# Revit family: result
name_source: partatom
category: Mechanical Equipment
units: mm (PartAtom-declared; Revit-internal decimal feet)

## family parameters
Always vertical = Yes
Cut with Voids When Loaded = No
Maintain Annotation Orientation = No
OmniClass Number = 23.75.00.00
OmniClass Title = Climate Control (HVAC)
Part Type = Normal
Room Calculation Point = No
Round Connector Dimension = Use Radius
Shared = No
Work Plane-Based = No

## types (1)
- -1-ALTAIR 120 V RE  - Heat Recovery Units
    AcquisitionDate = 0
    Arrangement = 0
    ArticleNumber = 0
    AssemblyPlace = 0
    AssessmentCondition = 0
    AssessmentDate = 0
    AssessmentDescription = 0
    AtmosphericAcidification = 0
    AtmosphericAcidificationPerUnit = 0
    Autor = Bimetica Parametric Design Services, S.L.
    BIMElementExpiryDate = 0
    BIMElementIssueDate = 2025-07-10
    BIMElementVersion = 1.0
    COBieCategory = 0
    ClimateChange = 0
    ClimateChangePerUnit = 0
    ConductorFunction = 0
    Connector Radius 1 = 47 mm  [stored 0.154199 ft]
    Connector Radius 2 = 47 mm  [stored 0.154199 ft]
    ContainerMaterial = 0
    CorrienteNominal = 0 A
    Default Elevation = 0 mm  [stored 0 ft]
    Description = Mechanical Ventilation Heat Recovery Unit with a high-efficiency heat exchanger to provide a constant supply of fresh tempered air into the living spaces.The incorporated intelligent humidity tracking control as standard, constantly monitor the humidity level, meaning no user intervention required.As humidity rises and falls, the motor speed adjusts in direct correlation.This controls IAQ quietly and efficiently, reducing the periods of time when the system operates on maximum speed, saving energy.Our constant flow technology delivers the required airflow at all times. The ultra compact design allows installation of the unit vertically on the wall.ALTAIR is equipped with high efficieny G4 filters for supply and extract.The included remote controller, allows the user to select the working mode of the unit (manual or automatic) and indicates when the filter needs replacing.It is advisable to use LAF silencers (accessory not included):&nbsp;LAF 95 for the ALTAIR-120 model.The ALTAIR unit can communicate with the home automation system via Modbus or other gateway protocols.By means of the SPCM Lite M communications board, the ALTAIR unit communicates with the CONNECTAIR platform, which allows it to be remotely controlled.Features- Counterflow heat exchanger with efficiency up to 88%.- Low consumption EC motor.- Centrifugal fans with forward bladed impeller.- Modbus connection.- EPP body.- 4 inlets Ø100 mm (ALTAIR 120).- Delivery filter:&nbsp;G4 (ISO coarse 65%).&nbsp;Optional M5 (ISO ePM10 50%).&nbsp;Extraction filter G4 (ISO coarse 65%).
    DiametroImpulsor = 0 mm  [stored 0 ft]
    Dimension 1 = Yes
    Dimension 2 = No
    DirectionOfRotation = 0
    DischargePosition = 0
    DischargePressureLoss = 0.0 Pa
    DischargeVelocity = 0.0 m/s
    DrivePowerLoss = 0 W
    EfficiencyCurve = 0
    Eutrophication = 0
    EutrophicationPerUnit = 0
    Exclusions = 0
    ExpectedServiceLife = 0
    FanEfficiency = 0
    FanPowerRate = 0 W
    HasProtectiveEarth = Yes
    HazardousWaste = 0
    HazardousWastePerUnit = 0
    IFCClassification = Fans
    IndiceFlujoNominal = 0.0 L/s
    IndicePotenciaNominal = 0 W
    InertWaste = 0
    InertWastePerUnit = 0
    InstallationDate = 0
    InsulationStandardClass = 0
    IsExtendedWarranty = No
    LifeCyclePhase = 0
    MaintenanceCertificate = 0
    MaintenanceCost = 0
    MaintenanceFrequency = 0
    MaintenanceRegulation = 0
    MaintenanceSpecifications = 0
    MaintenanceTask = 0
    MaintenanceUnit = 0
    Manufacturer = ELEKTRODESIGN VENTILATORY, SPOL.S.R.O.
    MasterformatCodigo = 23 00 00
    MasterformatTitulo = Heating, Ventilating, and Air Conditioning (HVAC)
    Material Carcasa = Steel, Galvanized painted white
    Material Conector Bornes = Plastic, Formed white
    MaterialHousing B = Steel, Galvanized painted black
    MaterialHousing C = Plastic, Formed Black
    MeanTimeBetweenFailure = 0
    Model = 0
    ModelLabel = 0
    NominalFrequencyRange = 0 Hz
    NonHazardousWaste = 0
    NonHazardousWastePerUnit = 0
    NonRenewableEnergyConsumption = 0
    NonRenewableEnergyConsumptionPerUnit = 0
    NumeroPolos = 1
    OmniclassCodigo = 23-33 31 19
    OmniclassTitulo = Fans
    OperationTemperatureRange = 0
    OperationalCriteria = 0
    OverallEfficiency = 0
    PA = 77 mm  [stored 0.252625 ft]
    PB = 360 mm  [stored 1.1811 ft]
    PC = 550 mm
    PCUT_INT = 84 mm  [stored 0.275591 ft]
    PCUT_INT2 = 84 mm  [stored 0.275591 ft]
    PD = 94 mm  [stored 0.308399 ft]
    PE = 30 mm  [stored 0.0984252 ft]
    PF = 660 mm
    PG = 850 mm  [stored 2.78871 ft]
    PH = 30 mm  [stored 0.0984252 ft]
    PII = 170 mm  [stored 0.557743 ft]
    PJ = 78 mm  [stored 0.255906 ft]
    PackingCareType = 0
    PesoBruto = 0.00 kg
    PhotochemicalOzoneFormation = 0
    PhotochemicalOzoneFormationPerUnit = 0
    PointOfContact = 0
    PowerFactor = 0.00%
    PresionDinamica = 0.0 Pa
    PresionEstaticaNominal = 0.0 Pa
    PresionTotalNominal = 0.0 Pa
    PressureCurve = 0
    ProductionYear = 0
    RadioactiveWaste = 0
    RadioactiveWastePerUnit = 0
    RenewableEnergyConsumption = 0
    RenewableEnergyConsumptionPerUnit = 0
    ResourceDepletion = 0
    ResourceDepletionPerUnit = 0
    SerialNumber = 0
    ServiceLifeDuration = 0
    ShaftPowerRate = 0 W
    SoundCurve = 0
    StratosphericOzoneLayerDestruction = 0
    StratosphericOzoneLayerDestructionPerUnit = 0
    Support Bracket Material = Steel, Galvanized
    TensionNominal = 0 V
    Throw Distance High Velocity = 0 mm  [stored 0 ft]
    Throw Distance Low Velocity = 0 mm  [stored 0 ft]
    Throw Distance Medium Velocity = 0
    TotalPrimaryEnergyConsumption = 0
    TotalPrimaryEnergyConsumptionPerUnit = 0
    Type Image = <None>
    UNSPSCCodigo = 40101604
    UNSPSCTitulo = Fans
    URL = https://www.solerpalau.com
    WarrantyContent = 0
    WarrantyEndDate = 0
    WarrantyStartDate = 0
    WaterConsumption = 0
    WaterConsumptionPerUnit = 0
    WheelTipSpeed = 0
    WrappingMaterial = 0
    spDI1 = 94 mm  [stored 0.308399 ft]
    spDO1 = 94 mm  [stored 0.308399 ft]
    spIntensidadMaximaAbsorbida = 0 A
    spPotenciaElectrica_Solucion = 0 W
    spPotenciaUtil_Solucion = 0 W
    spTamañoVentilador = 0 mm  [stored 0 ft]

note: [stored X ft] marks values corroborated as IEEE doubles in the binary element streams (Revit-internal decimal feet)
